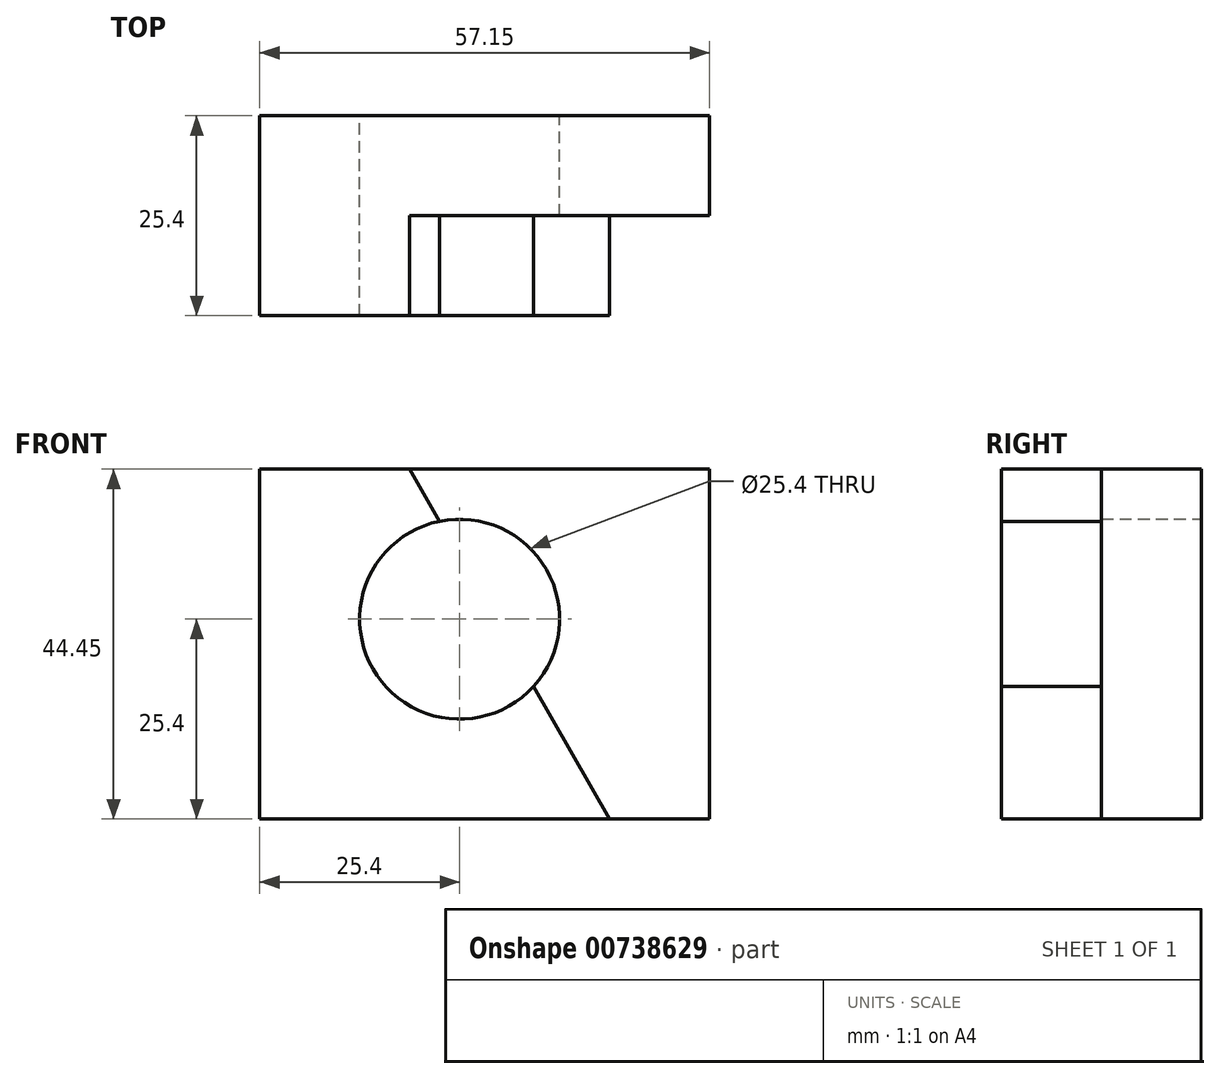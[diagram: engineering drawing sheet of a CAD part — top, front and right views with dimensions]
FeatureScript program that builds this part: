
annotation { "Feature Type Name" : "Feature", "Feature Type Description" : "" }
export const myFeature = defineFeature(function(context is Context, id is Id, definition is map)
    precondition{}
    {
        {
            var Q0;
            Q0=qCreatedBy(makeId("Front.planeOp"),FACE);
            var sketch = newSketch(context, id + "F0", { "sketchPlane" : qUnion([Q0])});
            skLineSegment(sketch, "E0.bottom", {"start": v(0, 0) * mm, "end": v(57.15, 0) * mm});
            skLineSegment(sketch, "E0.top", {"start": v(0, 44.45) * mm, "end": v(57.15, 44.45) * mm});
            skLineSegment(sketch, "E0.left", {"start": v(0, 0) * mm, "end": v(0, 44.45) * mm});
            skLineSegment(sketch, "E0.right", {"start": v(57.15, 0) * mm, "end": v(57.15, 44.45) * mm});
            skLineSegment(sketch, "E1", {"start": v(0, 0) * mm, "end": v(0, 25.4) * mm});
            skLineSegment(sketch, "E2", {"start": v(0, 25.4) * mm, "end": v(25.4, 25.4) * mm});
            skCircle(sketch, "E3", {"center": v(25.4, 25.4) * mm, "radius": 12.7 * mm});
            skSolve(sketch);
        }
        {
            var Q0;
            Q0=makeQuery(id+"F0.imprint","IMPRINT",FACE,{"disambiguationData":[TD([[makeQuery(id+"F0.imprint","IMPRINT",EDGE,{"derivedFrom":sQuery(id+"F0.wireOp",EDGE,"E0.bottom")}),1.0]])]});
            extrude(context, id + "F1", {"entities" : qUnion([Q0]), "depth" : 25.4 * mm, "offsetDistance" : 25.4 * mm});
        }
        {
            var Q0;
            Q0=makeQuery(id+"F1.opExtrude","CAP_FACE",FACE,{"disambiguationData":[OSD([sQuery(id+"F0.wireOp",EDGE,"E0.bottom"),sQuery(id+"F0.wireOp",EDGE,"E0.top"),sQuery(id+"F0.wireOp",EDGE,"E0.left"),sQuery(id+"F0.wireOp",EDGE,"E0.right"),sQuery(id+"F0.wireOp",EDGE,"E1"),sQuery(id+"F0.wireOp",EDGE,"E3")])],"isStart":false});
            var sketch = newSketch(context, id + "F2", { "sketchPlane" : qUnion([Q0])});
            skLineSegment(sketch, "E4", {"start": v(0, 44.45) * mm, "end": v(19.05, 44.45) * mm});
            skLineSegment(sketch, "E5", {"start": v(57.15, 0) * mm, "end": v(44.45, 0) * mm});
            skLineSegment(sketch, "E6", {"start": v(19.05, 44.45) * mm, "end": v(44.45, 0) * mm});
            skSolve(sketch);
        }
        {
            var Q0;
            {var subQ1=sQuery(id+"F2.wireOp",EDGE,"E5");Q0=makeQuery(id+"F2.imprint","IMPRINT",FACE,{"disambiguationData":[TD([[makeQuery(id+"F2.imprint","IMPRINT",EDGE,{"derivedFrom":subQ1}),1.0]])]});}
            extrude(context, id + "F3", {"entities" : qUnion([Q0]), "operationType" : NewBodyOperationType.REMOVE, "oppositeDirection" : true, "depth" : 12.7 * mm, "offsetDistance" : 25.4 * mm});
        }
    });
